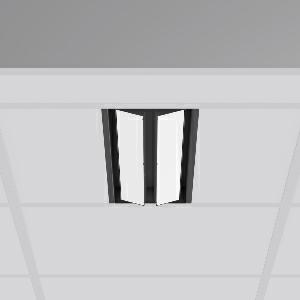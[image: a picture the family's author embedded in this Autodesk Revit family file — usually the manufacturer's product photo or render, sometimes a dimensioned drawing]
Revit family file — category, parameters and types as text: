
# Revit family: tx-move_901739_003_3_7303
name_source: partatom
category: Lighting Fixtures
units: mm (PartAtom-declared; Revit-internal decimal feet)

## family parameters
Cut with Voids When Loaded = No
Host = Face
Light Source = No
Part Type = Normal
Room Calculation Point = No
Round Connector Dimension = Use Diameter
Shared = No

## types (1)
- MultiLumen 1 (1 x LED Modul 835, 2450 lm, 3500)
    Apparent Load = 35 VA
    CIE Flux Codes = 47 79 96 100 100
    Color Rendering = 80
    Color Temperature = 3500
    Default Elevation = 1800 mm
    Description = Series: TX-MOVE
Einlege/Einbau-Flächenstrahler. Housing: sheet steel, powder-coated. 2xSwivel range: 90°. High-efficiency LED units with flush-mounted opal diffuser made of non-yellowing PMMA. Symmetrical wide beam light emission. Suitable for laying in grid ceiling module 625. Connected converter included in separate gearbox.Suitable for through-wiring.MultiLumen: Luminous flux adjustable in 3 steps. Accessories: Mounting frame for installation in suspended ceilings. Environmentally friendly and resource-saving due to replaceable and recyclable components. 
Colour: deep black, matt (RAL 9005)
Length: 622 mm
Width: 190 mm
Height: 39 mm
Cut-out length: 602 mm
Cut-out width: 174 mm
Recess height: 100 mm
Lamp: LED
Socket: without socket
Colour temperature: 3500K
Colour rendering index (CRI): 80
System power: 35 W
Rated luminous flux: 4900 lm
Luminous efficiency: 140 lm/W
System power 2: 47 W
Rated luminous flux 2: 6350 lm
Luminous efficiency 2: 135 lm/W
System power 3: 68 W
Rated luminous flux 3: 8650 lm
Luminous efficiency 3: 127 lm/W
Control gear: Regulated power supply
Protection class: I
Type of protection: IP 20
    Height = 0 mm  [stored 0 ft]
    Lamp = 1 x LED Modul 835
    Lamp Light Flux = 2450 lm
    Lamp count = 1
    Length = 622 mm
    Lifetime = 50000 h
    Luminous efficacy = 140 lm/W
    Manufacturer = RZB
    ModVariant = No
    Model = 901739.003.3
    Mounting Place = Ceiling, Wall
    Mounting Type = Recessed
    Number of Poles = 1
    OnlyDefault = Yes
    Power Factor = 1
    Product Name = TX-MOVE
    Product group = Recessed projectors
    ProductGroupID = 401
    Protection Class = Protection class I
    Protection Degree = IP 20
    RLX_Detail_Level = 1
    RLX_Emergency_Light_Flux = 0 lm
    RLX_Emergency_Type = 0
    RLX_Emergency_Type_DB = No
    RlxData = <blob elided: 31545 chars, md5=cab56f63>
    Socket = socket
    Standby Power = 0 W
    System Light Flux = 4900 lm
    System Power = 35 W
    Type Comments = MultiLumen 1
    Type Image = 901739.003.jpg
    URL = http://relux.com
    VarID = multilumen_1
    Voltage = 230 V
    Voltage Range = 220-240 V
    Weight = 0.00 kg
    Width = 190 mm  [stored 0.62336 ft]

note: [stored X ft] marks values corroborated as IEEE doubles in the binary element streams (Revit-internal decimal feet)

## geometry (parser evidence)
native form markers: Blend x4, Sweep x16
no freeform markers — native parametric forms only
